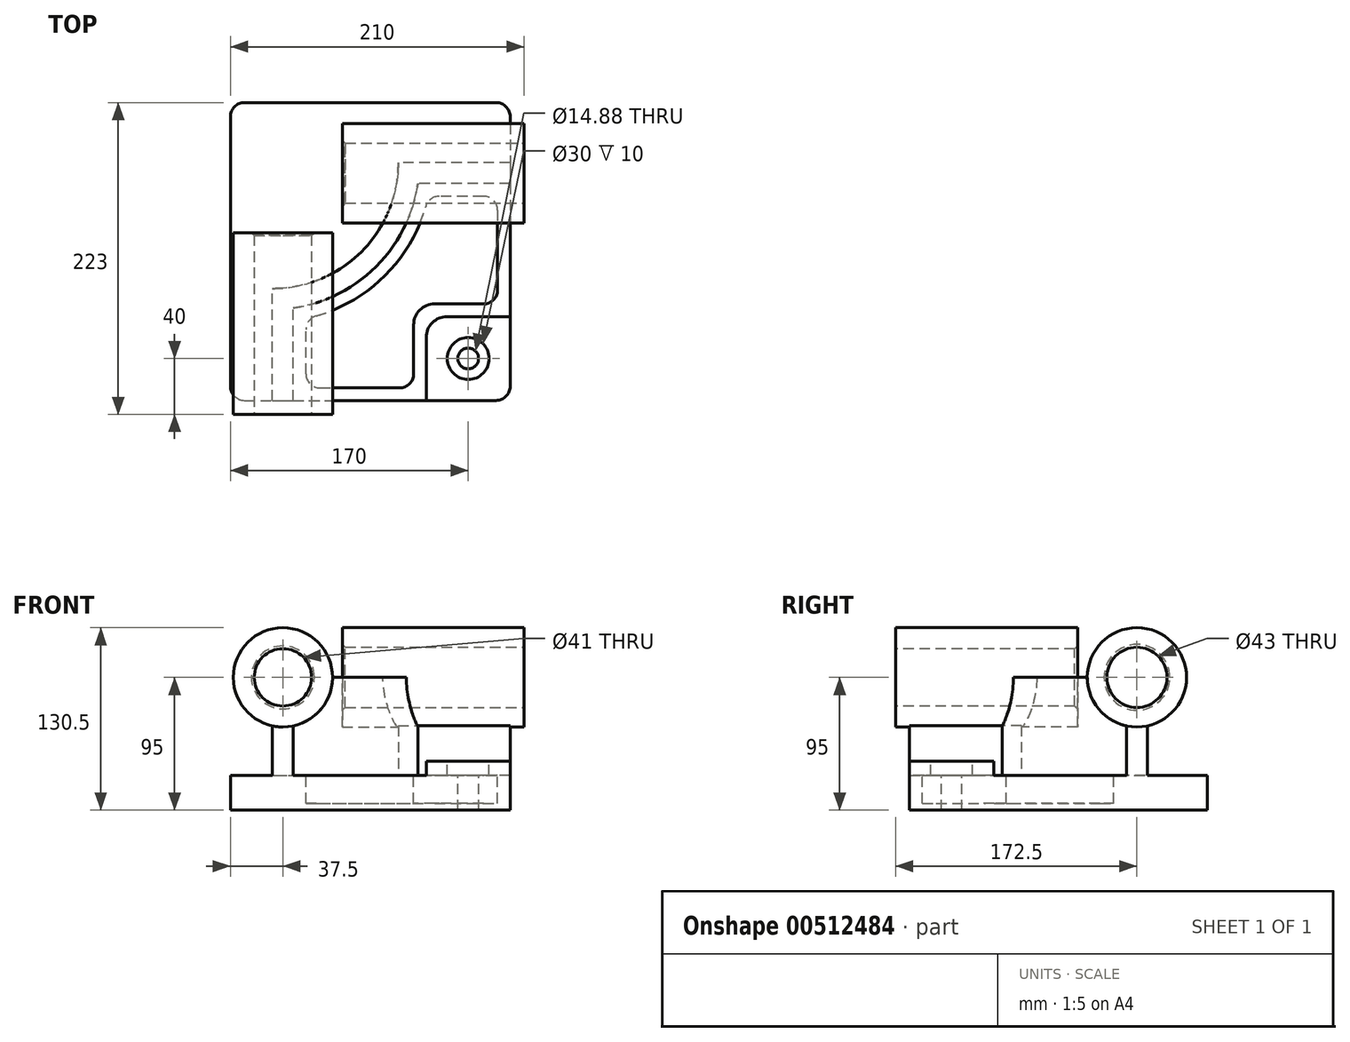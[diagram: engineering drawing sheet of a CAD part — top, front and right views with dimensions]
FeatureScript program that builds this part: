
annotation { "Feature Type Name" : "Feature", "Feature Type Description" : "" }
export const myFeature = defineFeature(function(context is Context, id is Id, definition is map)
    precondition{}
    {
        {
            var Q0;
            Q0=qCreatedBy(makeId("Top.planeOp"),FACE);
            var sketch = newSketch(context, id + "F0", { "sketchPlane" : qUnion([Q0])});
            skLineSegment(sketch, "E0.bottom", {"start": v(-90, 106.5) * mm, "end": v(90, 106.5) * mm});
            skLineSegment(sketch, "E0.top", {"start": v(-90, -106.5) * mm, "end": v(90, -106.5) * mm});
            skLineSegment(sketch, "E0.left", {"start": v(-100, 96.5) * mm, "end": v(-100, -96.5) * mm});
            skLineSegment(sketch, "E0.right", {"start": v(100, 96.5) * mm, "end": v(100, -96.5) * mm});
            skPoint(sketch, "E1.visualSharp", {"position": v(100, 106.5) * mm});
            skArc(sketch, "E1.filletArc", {"start": v(100, 96.5) * mm, "mid": v(97.07, 103.57) * mm, "end": v(90, 106.5) * mm});
            skPoint(sketch, "E2.visualSharp", {"position": v(100, -106.5) * mm});
            skArc(sketch, "E2.filletArc", {"start": v(90, -106.5) * mm, "mid": v(97.07, -103.57) * mm, "end": v(100, -96.5) * mm});
            skPoint(sketch, "E3.visualSharp", {"position": v(-100, -106.5) * mm});
            skArc(sketch, "E3.filletArc", {"start": v(-100, -96.5) * mm, "mid": v(-97.07, -103.57) * mm, "end": v(-90, -106.5) * mm});
            skPoint(sketch, "E4.visualSharp", {"position": v(-100, 106.5) * mm});
            skArc(sketch, "E4.filletArc", {"start": v(-90, 106.5) * mm, "mid": v(-97.07, 103.57) * mm, "end": v(-100, 96.5) * mm});
            skSolve(sketch);
        }
        {
            var Q0;
            Q0 = qSketchRegion(id + "F0", true);
            extrude(context, id + "F1", {"entities" : qUnion([Q0]), "oppositeDirection" : true, "depth" : 25 * mm});
        }
        {
            var Q0;
            Q0=makeQuery(id+"F1.opExtrude","CAP_FACE",FACE,{"disambiguationData":[OSD([sQuery(id+"F0.wireOp",EDGE,"E0.bottom"),sQuery(id+"F0.wireOp",EDGE,"E0.top"),sQuery(id+"F0.wireOp",EDGE,"E0.left"),sQuery(id+"F0.wireOp",EDGE,"E0.right"),sQuery(id+"F0.wireOp",EDGE,"E1.filletArc"),sQuery(id+"F0.wireOp",EDGE,"E2.filletArc"),sQuery(id+"F0.wireOp",EDGE,"E3.filletArc"),sQuery(id+"F0.wireOp",EDGE,"E4.filletArc")])],"isStart":true});
            var sketch = newSketch(context, id + "F2", { "sketchPlane" : qUnion([Q0])});
            skLineSegment(sketch, "E5", {"start": v(-70, -106.5) * mm, "end": v(-70, -26.5) * mm});
            skLineSegment(sketch, "E6", {"start": v(100, 63.5) * mm, "end": v(20, 63.5) * mm});
            skLineSegment(sketch, "E7", {"start": v(20, 63.5) * mm, "end": v(-79.42, 63.5) * mm, "construction": true});
            skLineSegment(sketch, "E8", {"start": v(-70, -26.5) * mm, "end": v(-70, 69.36) * mm, "construction": true});
            skArc(sketch, "E9", {"start": v(-70, -26.5) * mm, "mid": v(-6.36, -0.14) * mm, "end": v(20, 63.5) * mm});
            skLineSegment(sketch, "E10.0", {"start": v(100, 48.5) * mm, "end": v(33.92, 48.5) * mm});
            skArc(sketch, "E11.0", {"start": v(-55, -40.42) * mm, "mid": v(4.25, -10.75) * mm, "end": v(33.92, 48.5) * mm});
            skLineSegment(sketch, "E12.0", {"start": v(-55, -106.5) * mm, "end": v(-55, -40.42) * mm});
            skLineSegment(sketch, "E13", {"start": v(-70, -106.5) * mm, "end": v(-55, -106.5) * mm});
            skLineSegment(sketch, "E14", {"start": v(100, 63.5) * mm, "end": v(100, 48.5) * mm});
            skSolve(sketch);
        }
        {
            var Q0;
            Q0 = qSketchRegion(id + "F2", true);
            extrude(context, id + "F3", {"entities" : qUnion([Q0]), "operationType" : NewBodyOperationType.ADD, "depth" : 70 * mm});
        }
        {
            var Q0;
            {var subQ0=sQuery(id+"F0.wireOp",EDGE,"E2.filletArc");var subQ1=sQuery(id+"F0.wireOp",EDGE,"E0.right");var subQ2=sQuery(id+"F0.wireOp",EDGE,"E0.top");Q0=makeQuery(id+"F3.boolean.opBoolean","SPLIT",FACE,{"disambiguationData":[TD([makeQuery(id+"F1.opExtrude","SWEPT_FACE",FACE,{"disambiguationData":[OSD([subQ0])]})])],"derivedFrom":makeQuery(id+"F1.opExtrude","CAP_FACE",FACE,{"disambiguationData":[OSD([sQuery(id+"F0.wireOp",EDGE,"E0.bottom"),subQ2,sQuery(id+"F0.wireOp",EDGE,"E0.left"),subQ1,sQuery(id+"F0.wireOp",EDGE,"E1.filletArc"),subQ0,sQuery(id+"F0.wireOp",EDGE,"E3.filletArc"),sQuery(id+"F0.wireOp",EDGE,"E4.filletArc")])],"isStart":true})});}
            var sketch = newSketch(context, id + "F4", { "sketchPlane" : qUnion([Q0])});
            skLineSegment(sketch, "E15", {"start": v(100, -46.5) * mm, "end": v(55, -46.5) * mm});
            skLineSegment(sketch, "E16", {"start": v(40, -61.5) * mm, "end": v(40, -106.5) * mm});
            skLineSegment(sketch, "E17", {"start": v(100, -46.5) * mm, "end": v(100, -96.5) * mm});
            skLineSegment(sketch, "E18", {"start": v(90, -106.5) * mm, "end": v(40, -106.5) * mm});
            skPoint(sketch, "E19.visualSharp", {"position": v(100, -106.5) * mm});
            skArc(sketch, "E19.filletArc", {"start": v(90, -106.5) * mm, "mid": v(97.07, -103.57) * mm, "end": v(100, -96.5) * mm});
            skPoint(sketch, "E20.visualSharp", {"position": v(40, -46.5) * mm});
            skArc(sketch, "E20.filletArc", {"start": v(55, -46.5) * mm, "mid": v(44.4, -50.9) * mm, "end": v(40, -61.5) * mm});
            skSolve(sketch);
        }
        {
            var Q0;
            Q0 = qSketchRegion(id + "F4", true);
            extrude(context, id + "F5", {"entities" : qUnion([Q0]), "operationType" : NewBodyOperationType.ADD, "depth" : 10 * mm});
        }
        {
            var Q0;
            Q0=makeQuery(id+"F5.opExtrude","CAP_FACE",FACE,{"disambiguationData":[OSD([sQuery(id+"F4.wireOp",EDGE,"E15"),sQuery(id+"F4.wireOp",EDGE,"E16"),sQuery(id+"F4.wireOp",EDGE,"E17"),sQuery(id+"F4.wireOp",EDGE,"E18"),sQuery(id+"F4.wireOp",EDGE,"E19.filletArc"),sQuery(id+"F4.wireOp",EDGE,"E20.filletArc")])],"isStart":false});
            var sketch = newSketch(context, id + "F6", { "sketchPlane" : qUnion([Q0])});
            skCircle(sketch, "E21", {"center": v(70, -76.5) * mm, "radius": 7.44 * mm});
            skSolve(sketch);
        }
        {
            var Q0;
            Q0 = qSketchRegion(id + "F6", true);
            extrude(context, id + "F7", {"entities" : qUnion([Q0]), "operationType" : NewBodyOperationType.REMOVE, "endBound" : BoundingType.THROUGH_ALL, "oppositeDirection" : true, "depth" : 25 * mm});
        }
        {
            var Q0;
            Q0=makeQuery(id+"F5.opExtrude","CAP_FACE",FACE,{"disambiguationData":[OSD([sQuery(id+"F4.wireOp",EDGE,"E15"),sQuery(id+"F4.wireOp",EDGE,"E16"),sQuery(id+"F4.wireOp",EDGE,"E17"),sQuery(id+"F4.wireOp",EDGE,"E18"),sQuery(id+"F4.wireOp",EDGE,"E19.filletArc"),sQuery(id+"F4.wireOp",EDGE,"E20.filletArc")])],"isStart":false});
            var sketch = newSketch(context, id + "F8", { "sketchPlane" : qUnion([Q0])});
            skCircle(sketch, "E22", {"center": v(70, -76.5) * mm, "radius": 15 * mm});
            skSolve(sketch);
        }
        {
            var Q0;
            Q0 = qSketchRegion(id + "F8", true);
            extrude(context, id + "F9", {"entities" : qUnion([Q0]), "operationType" : NewBodyOperationType.REMOVE, "oppositeDirection" : true, "depth" : 10 * mm});
        }
        {
            var Q0;
            {var subQ0=sQuery(id+"F0.wireOp",EDGE,"E2.filletArc");var subQ1=sQuery(id+"F0.wireOp",EDGE,"E0.right");var subQ2=sQuery(id+"F0.wireOp",EDGE,"E0.top");Q0=makeQuery(id+"F3.boolean.opBoolean","SPLIT",FACE,{"disambiguationData":[TD([makeQuery(id+"F1.opExtrude","SWEPT_FACE",FACE,{"disambiguationData":[OSD([subQ0])]})])],"derivedFrom":makeQuery(id+"F1.opExtrude","CAP_FACE",FACE,{"disambiguationData":[OSD([sQuery(id+"F0.wireOp",EDGE,"E0.bottom"),subQ2,sQuery(id+"F0.wireOp",EDGE,"E0.left"),subQ1,sQuery(id+"F0.wireOp",EDGE,"E1.filletArc"),subQ0,sQuery(id+"F0.wireOp",EDGE,"E3.filletArc"),sQuery(id+"F0.wireOp",EDGE,"E4.filletArc")])],"isStart":true})});}
            var sketch = newSketch(context, id + "F10", { "sketchPlane" : qUnion([Q0])});
            skLineSegment(sketch, "E23", {"start": v(81, 39.5) * mm, "end": v(49.25, 39.5) * mm});
            skLineSegment(sketch, "E24", {"start": v(91, 29.5) * mm, "end": v(91, -27.5) * mm});
            skLineSegment(sketch, "E25", {"start": v(-46, -87.5) * mm, "end": v(-46, -55.75) * mm});
            skLineSegment(sketch, "E26", {"start": v(-36, -97.5) * mm, "end": v(21, -97.5) * mm});
            skLineSegment(sketch, "E27", {"start": v(31, -87.5) * mm, "end": v(31, -52.5) * mm});
            skLineSegment(sketch, "E28", {"start": v(46, -37.5) * mm, "end": v(81, -37.5) * mm});
            skArc(sketch, "E29.0", {"start": v(-38.74, -46.13) * mm, "mid": v(10.61, -17.11) * mm, "end": v(39.63, 32.24) * mm});
            skArc(sketch, "E30.filletArc", {"start": v(46, -37.5) * mm, "mid": v(35.4, -41.9) * mm, "end": v(31, -52.5) * mm});
            skArc(sketch, "E31.filletArc", {"start": v(21, -97.5) * mm, "mid": v(28.07, -94.57) * mm, "end": v(31, -87.5) * mm});
            skArc(sketch, "E32.filletArc", {"start": v(-46, -87.5) * mm, "mid": v(-43.07, -94.57) * mm, "end": v(-36, -97.5) * mm});
            skArc(sketch, "E33.filletArc", {"start": v(-38.74, -46.13) * mm, "mid": v(-43.98, -49.72) * mm, "end": v(-46, -55.75) * mm});
            skArc(sketch, "E34.filletArc", {"start": v(81, -37.5) * mm, "mid": v(88.07, -34.57) * mm, "end": v(91, -27.5) * mm});
            skArc(sketch, "E35.filletArc", {"start": v(91, 29.5) * mm, "mid": v(88.07, 36.57) * mm, "end": v(81, 39.5) * mm});
            skArc(sketch, "E36.filletArc", {"start": v(49.25, 39.5) * mm, "mid": v(43.22, 37.48) * mm, "end": v(39.63, 32.24) * mm});
            skSolve(sketch);
        }
        {
            var Q0;
            Q0 = qSketchRegion(id + "F10", true);
            extrude(context, id + "F11", {"entities" : qUnion([Q0]), "operationType" : NewBodyOperationType.REMOVE, "oppositeDirection" : true, "depth" : 20 * mm});
        }
        {
            var Q0;
            Q0=makeQuery(id+"F5.boolean.opBoolean","MERGE",FACE,{"derivedFrom":[makeQuery(id+"F3.boolean.opBoolean","MERGE",FACE,{"derivedFrom":[makeQuery(id+"F1.opExtrude","SWEPT_FACE",FACE,{"disambiguationData":[OSD([sQuery(id+"F0.wireOp",EDGE,"E0.right")])]}),makeQuery(id+"F3.opExtrude","SWEPT_FACE",FACE,{"disambiguationData":[OSD([sQuery(id+"F2.wireOp",EDGE,"E14")])]})]}),makeQuery(id+"F5.opExtrude","SWEPT_FACE",FACE,{"disambiguationData":[OSD([sQuery(id+"F4.wireOp",EDGE,"E17")])]})]});
            cPlane(context, id + "F12", {"entities" : qUnion([Q0]), "cplaneType" : CPlaneType.OFFSET, "offset" : 10 * mm, "width" : 150 * mm, "height" : 150 * mm});
        }
        {
            var Q0;
            Q0=qCreatedBy(id+"F12.planeOp",FACE);
            var sketch = newSketch(context, id + "F13", { "sketchPlane" : qUnion([Q0])});
            skLineSegment(sketch, "E37", {"start": v(56, -25) * mm, "end": v(56, 70) * mm, "construction": true});
            skCircle(sketch, "E38", {"center": v(56, 70) * mm, "radius": 35.5 * mm});
            skSolve(sketch);
        }
        {
            var Q0;
            Q0 = qSketchRegion(id + "F13", true);
            extrude(context, id + "F14", {"entities" : qUnion([Q0]), "operationType" : NewBodyOperationType.ADD, "oppositeDirection" : true, "depth" : 130 * mm});
        }
        {
            var Q0;
            Q0=makeQuery(id+"F14.opExtrude","CAP_FACE",FACE,{"disambiguationData":[OSD([sQuery(id+"F13.wireOp",EDGE,"E38")])],"isStart":true});
            var sketch = newSketch(context, id + "F15", { "sketchPlane" : qUnion([Q0])});
            skCircle(sketch, "E39", {"center": v(56, 70) * mm, "radius": 21.5 * mm});
            skSolve(sketch);
        }
        {
            var Q0;
            Q0 = qSketchRegion(id + "F15", true);
            extrude(context, id + "F16", {"entities" : qUnion([Q0]), "operationType" : NewBodyOperationType.REMOVE, "endBound" : BoundingType.THROUGH_ALL, "oppositeDirection" : true, "depth" : 25 * mm});
        }
        {
            var Q0;
            Q0=makeQuery(id+"F5.boolean.opBoolean","MERGE",FACE,{"derivedFrom":[makeQuery(id+"F3.boolean.opBoolean","MERGE",FACE,{"derivedFrom":[makeQuery(id+"F1.opExtrude","SWEPT_FACE",FACE,{"disambiguationData":[OSD([sQuery(id+"F0.wireOp",EDGE,"E0.top")])]}),makeQuery(id+"F3.opExtrude","SWEPT_FACE",FACE,{"disambiguationData":[OSD([sQuery(id+"F2.wireOp",EDGE,"E13")])]})]}),makeQuery(id+"F5.opExtrude","SWEPT_FACE",FACE,{"disambiguationData":[OSD([sQuery(id+"F4.wireOp",EDGE,"E18")])]})]});
            cPlane(context, id + "F17", {"entities" : qUnion([Q0]), "cplaneType" : CPlaneType.OFFSET, "offset" : 10 * mm, "width" : 150 * mm, "height" : 150 * mm});
        }
        {
            var Q0;
            Q0=qCreatedBy(id+"F17.planeOp",FACE);
            var sketch = newSketch(context, id + "F18", { "sketchPlane" : qUnion([Q0])});
            skLineSegment(sketch, "E40", {"start": v(-62.5, -25) * mm, "end": v(-62.5, 70) * mm, "construction": true});
            skCircle(sketch, "E41", {"center": v(-62.5, 70) * mm, "radius": 35.5 * mm});
            skSolve(sketch);
        }
        {
            var Q0;
            Q0 = qSketchRegion(id + "F18", true);
            extrude(context, id + "F19", {"entities" : qUnion([Q0]), "operationType" : NewBodyOperationType.ADD, "oppositeDirection" : true, "depth" : 130 * mm});
        }
        {
            var Q0;
            Q0=makeQuery(id+"F19.opExtrude","CAP_FACE",FACE,{"disambiguationData":[OSD([sQuery(id+"F18.wireOp",EDGE,"E41")])],"isStart":true});
            var sketch = newSketch(context, id + "F20", { "sketchPlane" : qUnion([Q0])});
            skCircle(sketch, "E42", {"center": v(-62.5, 70) * mm, "radius": 20.5 * mm});
            skSolve(sketch);
        }
        {
            var Q0;
            Q0 = qSketchRegion(id + "F20", true);
            extrude(context, id + "F21", {"entities" : qUnion([Q0]), "operationType" : NewBodyOperationType.REMOVE, "endBound" : BoundingType.THROUGH_ALL, "oppositeDirection" : true, "depth" : 25 * mm});
        }
        {
            var Q0;
            Q0=makeQuery(id+"F21.boolean.opBoolean","COPY",EDGE,{"derivedFrom":makeQuery(id+"F21.opExtrude","CAP_EDGE",EDGE,{"disambiguationData":[OSD([sQuery(id+"F20.wireOp",EDGE,"E42")])],"isStart":true})});
            var Q1;
            Q1=makeQuery(id+"F21.boolean.opBoolean","INTERSECT",EDGE,{"derivedFrom":[makeQuery(id+"F19.opExtrude","CAP_FACE",FACE,{"disambiguationData":[OSD([sQuery(id+"F18.wireOp",EDGE,"E41")])],"isStart":false}),makeQuery(id+"F21.opExtrude","SWEPT_FACE",FACE,{"disambiguationData":[OSD([sQuery(id+"F20.wireOp",EDGE,"E42")])]})]});
            var Q2;
            Q2=makeQuery(id+"F16.boolean.opBoolean","INTERSECT",EDGE,{"derivedFrom":[makeQuery(id+"F14.opExtrude","CAP_FACE",FACE,{"disambiguationData":[OSD([sQuery(id+"F13.wireOp",EDGE,"E38")])],"isStart":false}),makeQuery(id+"F16.opExtrude","SWEPT_FACE",FACE,{"disambiguationData":[OSD([sQuery(id+"F15.wireOp",EDGE,"E39")])]})]});
            var Q3;
            Q3=makeQuery(id+"F16.boolean.opBoolean","COPY",EDGE,{"derivedFrom":makeQuery(id+"F16.opExtrude","CAP_EDGE",EDGE,{"disambiguationData":[OSD([sQuery(id+"F15.wireOp",EDGE,"E39")])],"isStart":true})});
            chamfer(context, id + "F22", {"entities" : qUnion([Q0, Q1, Q2, Q3]), "width" : 2 * mm, "tangentPropagation" : true});
        }
    });
